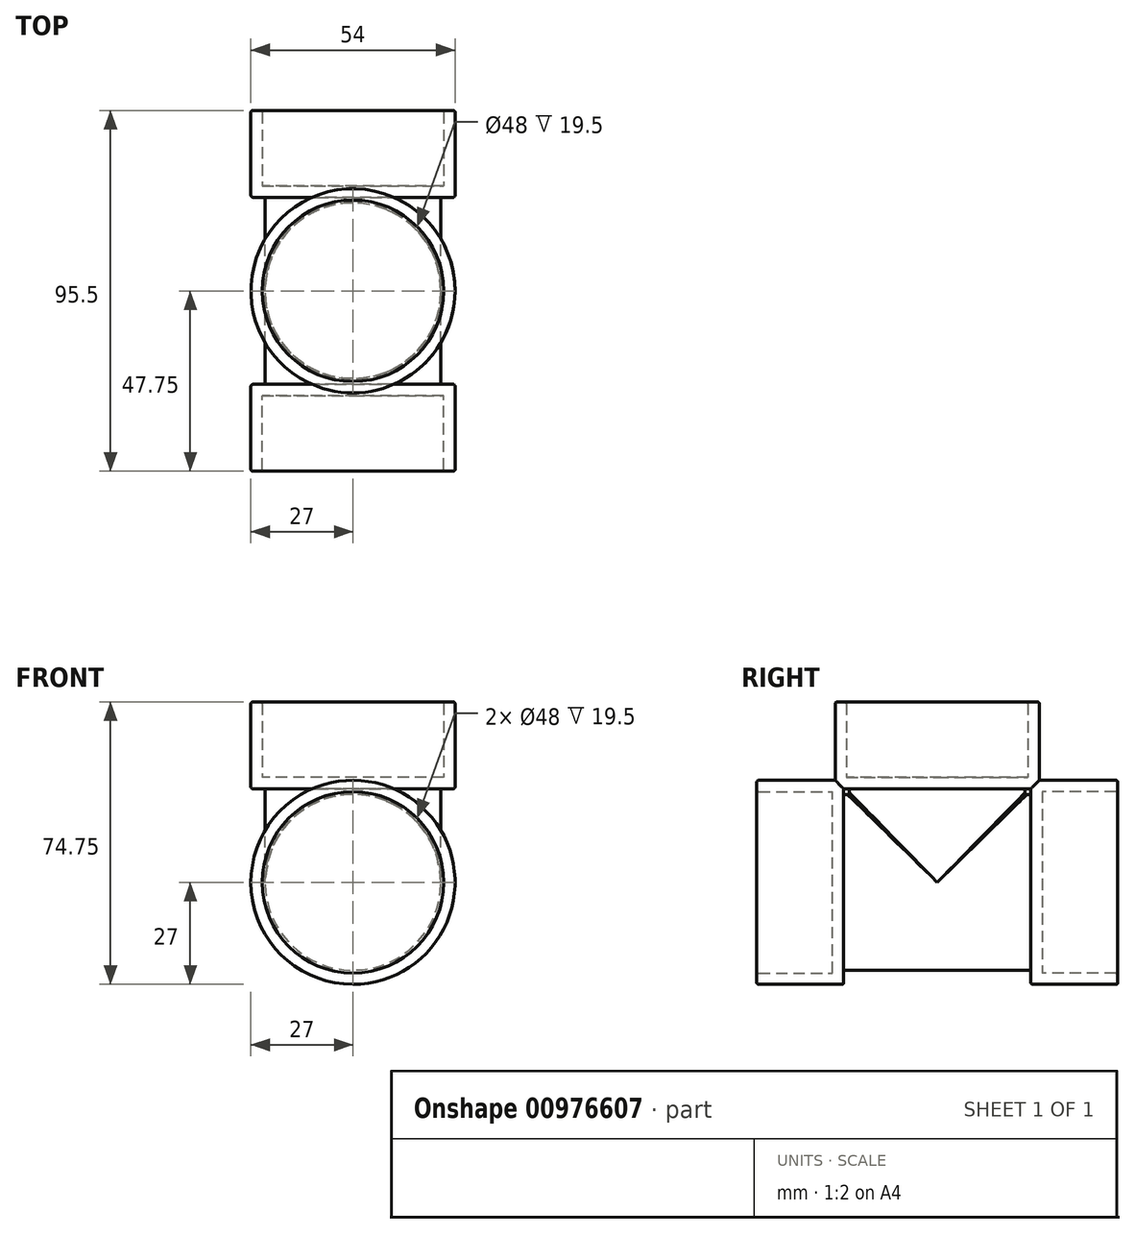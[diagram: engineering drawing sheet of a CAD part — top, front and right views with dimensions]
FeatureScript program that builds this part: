
annotation { "Feature Type Name" : "Feature", "Feature Type Description" : "" }
export const myFeature = defineFeature(function(context is Context, id is Id, definition is map)
    precondition{}
    {
        {
            var Q0;
            Q0=qCreatedBy(makeId("Right.planeOp"),FACE);
            var sketch = newSketch(context, id + "F0", { "sketchPlane" : qUnion([Q0])});
            skLineSegment(sketch, "E0.bottom", {"start": v(-22.5, 23.25) * mm, "end": v(-24, 23.25) * mm});
            skLineSegment(sketch, "E0.right", {"start": v(-24, 23.25) * mm, "end": v(-24, -23.25) * mm});
            skPoint(sketch, "E0.middle", {"position": v(0, 0) * mm});
            skLineSegment(sketch, "E1.top", {"start": v(24, 24.75) * mm, "end": v(-22.5, 24.75) * mm});
            skLineSegment(sketch, "E1.left", {"start": v(24, 23.25) * mm, "end": v(24, 24.75) * mm});
            skLineSegment(sketch, "E1.right", {"start": v(-22.5, 23.25) * mm, "end": v(-22.5, 24.75) * mm});
            skPoint(sketch, "E1.bottom.start.orphan", {"position": v(24, -23.25) * mm});
            skLineSegment(sketch, "E2", {"start": v(24, 23.25) * mm, "end": v(25.5, 23.25) * mm});
            skLineSegment(sketch, "E3", {"start": v(25.5, 23.25) * mm, "end": v(25.5, -23.25) * mm});
            skLineSegment(sketch, "E4", {"start": v(-24, -23.25) * mm, "end": v(25.5, -23.25) * mm});
            skSolve(sketch);
        }
        {
            var Q0;
            Q0=makeQuery(id+"F0.imprint","IMPRINT",FACE,{"disambiguationData":[TD([[makeQuery(id+"F0.imprint","IMPRINT",EDGE,{"derivedFrom":sQuery(id+"F0.wireOp",EDGE,"E0.bottom")}),1.0]])]});
            extrude(context, id + "F1", {"entities" : qUnion([Q0]), "depth" : 46.5 * mm, "offsetDistance" : 25 * mm});
        }
        {
            var Q0;
            Q0=makeQuery(id+"F1.opExtrude","CAP_EDGE",EDGE,{"disambiguationData":[OSD([sQuery(id+"F0.wireOp",EDGE,"E1.right")])],"isStart":false});
            var Q1;
            Q1=makeQuery(id+"F1.opExtrude","CAP_EDGE",EDGE,{"disambiguationData":[OSD([sQuery(id+"F0.wireOp",EDGE,"E0.bottom")])],"isStart":false});
            var Q2;
            Q2=makeQuery(id+"F1.opExtrude","CAP_EDGE",EDGE,{"disambiguationData":[OSD([sQuery(id+"F0.wireOp",EDGE,"E0.bottom")])],"isStart":true});
            var Q3;
            Q3=makeQuery(id+"F1.opExtrude","CAP_EDGE",EDGE,{"disambiguationData":[OSD([sQuery(id+"F0.wireOp",EDGE,"E1.right")])],"isStart":true});
            var Q4;
            Q4=makeQuery(id+"F1.opExtrude","CAP_EDGE",EDGE,{"disambiguationData":[OSD([sQuery(id+"F0.wireOp",EDGE,"E0.top"),sQuery(id+"F0.wireOp",EDGE,"E1.bottom")])],"isStart":true});
            var Q5;
            Q5=makeQuery(id+"F1.opExtrude","CAP_EDGE",EDGE,{"disambiguationData":[OSD([sQuery(id+"F0.wireOp",EDGE,"E1.left")])],"isStart":true});
            var Q6;
            Q6=makeQuery(id+"F1.opExtrude","CAP_EDGE",EDGE,{"disambiguationData":[OSD([sQuery(id+"F0.wireOp",EDGE,"E1.left")])],"isStart":false});
            var Q7;
            Q7=makeQuery(id+"F1.opExtrude","CAP_EDGE",EDGE,{"disambiguationData":[OSD([sQuery(id+"F0.wireOp",EDGE,"E0.top"),sQuery(id+"F0.wireOp",EDGE,"E1.bottom")])],"isStart":false});
            var Q8;
            Q8=makeQuery(id+"F1.opExtrude","CAP_EDGE",EDGE,{"disambiguationData":[OSD([sQuery(id+"F0.wireOp",EDGE,"rKhK8Vj8-QIDx-pT06-vwu7-Rd0EUUnwVlHf")])],"isStart":false});
            var Q9;
            Q9=makeQuery(id+"F1.opExtrude","CAP_EDGE",EDGE,{"disambiguationData":[OSD([sQuery(id+"F0.wireOp",EDGE,"rKhK8Vj8-QIDx-pT06-vwu7-Rd0EUUnwVlHf")])],"isStart":true});
            var Q10;
            Q10=makeQuery(id+"F1.opExtrude","CAP_EDGE",EDGE,{"disambiguationData":[OSD([sQuery(id+"F0.wireOp",EDGE,"E2")])],"isStart":true});
            var Q11;
            Q11=makeQuery(id+"F1.opExtrude","CAP_EDGE",EDGE,{"disambiguationData":[OSD([sQuery(id+"F0.wireOp",EDGE,"E2")])],"isStart":false});
            var Q12;
            Q12=makeQuery(id+"F1.opExtrude","CAP_EDGE",EDGE,{"disambiguationData":[OSD([sQuery(id+"F0.wireOp",EDGE,"E4")])],"isStart":false});
            var Q13;
            Q13=makeQuery(id+"F1.opExtrude","CAP_EDGE",EDGE,{"disambiguationData":[OSD([sQuery(id+"F0.wireOp",EDGE,"E4")])],"isStart":true});
            fillet(context, id + "F2", {"entities" : qUnion([Q0, Q1, Q2, Q3, Q4, Q5, Q6, Q7, Q8, Q9, Q10, Q11, Q12, Q13]), "radius" : 23.25 * mm, "tangentPropagation" : true, "allowEdgeOverflow" : false});
        }
        {
            var Q0;
            Q0=makeQuery(id+"F1.opExtrude","SWEPT_FACE",FACE,{"disambiguationData":[OSD([sQuery(id+"F0.wireOp",EDGE,"E1.top")])]});
            var sketch = newSketch(context, id + "F3", { "sketchPlane" : qUnion([Q0])});
            skCircle(sketch, "E5", {"center": v(23.25, 0.75) * mm, "radius": 27 * mm});
            skCircle(sketch, "E6", {"center": v(23.25, 0.75) * mm, "radius": 24 * mm});
            skCircle(sketch, "E7", {"center": v(23.25, 0.75) * mm, "radius": 20 * mm});
            skSolve(sketch);
        }
        {
            var Q0;
            Q0=makeQuery(id+"F1.opExtrude","SWEPT_FACE",FACE,{"disambiguationData":[OSD([sQuery(id+"F0.wireOp",EDGE,"E0.right")])]});
            var sketch = newSketch(context, id + "F4", { "sketchPlane" : qUnion([Q0])});
            skCircle(sketch, "E8", {"center": v(23.25, 0) * mm, "radius": 27 * mm});
            skCircle(sketch, "E9", {"center": v(23.25, 0) * mm, "radius": 24 * mm});
            skCircle(sketch, "E10", {"center": v(23.25, 0) * mm, "radius": 20 * mm});
            skSolve(sketch);
        }
        {
            var Q0;
            Q0=makeQuery(id+"F3.imprint","IMPRINT",FACE,{"disambiguationData":[TD([[makeQuery(id+"F3.imprint","IMPRINT",EDGE,{"derivedFrom":sQuery(id+"F3.wireOp",EDGE,"E7")}),-1.0]])]});
            var Q1;
            Q1=makeQuery(id+"F3.imprint","IMPRINT",FACE,{"disambiguationData":[TD([[makeQuery(id+"F3.imprint","IMPRINT",EDGE,{"derivedFrom":sQuery(id+"F3.wireOp",EDGE,"E6")}),1.0]])]});
            extrude(context, id + "F5", {"entities" : qUnion([Q0, Q1]), "operationType" : NewBodyOperationType.ADD, "depth" : 3 * mm, "offsetDistance" : 25 * mm});
        }
        {
            var Q0;
            Q0=makeQuery(id+"F3.imprint","IMPRINT",FACE,{"disambiguationData":[TD([[makeQuery(id+"F3.imprint","IMPRINT",EDGE,{"derivedFrom":sQuery(id+"F3.wireOp",EDGE,"E5")}),1.0]])]});
            extrude(context, id + "F6", {"entities" : qUnion([Q0]), "operationType" : NewBodyOperationType.ADD, "depth" : 23 * mm, "offsetDistance" : 25 * mm});
        }
        {
            var Q0;
            Q0=makeQuery(id+"F4.imprint","IMPRINT",FACE,{"disambiguationData":[TD([[makeQuery(id+"F4.imprint","IMPRINT",EDGE,{"derivedFrom":sQuery(id+"F4.wireOp",EDGE,"E10")}),-1.0]])]});
            var Q1;
            Q1=makeQuery(id+"F4.imprint","IMPRINT",FACE,{"disambiguationData":[TD([[makeQuery(id+"F4.imprint","IMPRINT",EDGE,{"derivedFrom":sQuery(id+"F4.wireOp",EDGE,"E9")}),1.0]])]});
            extrude(context, id + "F7", {"entities" : qUnion([Q0, Q1]), "operationType" : NewBodyOperationType.ADD, "depth" : 3 * mm, "offsetDistance" : 25 * mm});
        }
        {
            var Q0;
            Q0=makeQuery(id+"F4.imprint","IMPRINT",FACE,{"disambiguationData":[TD([[makeQuery(id+"F4.imprint","IMPRINT",EDGE,{"derivedFrom":sQuery(id+"F4.wireOp",EDGE,"E8")}),1.0]])]});
            extrude(context, id + "F8", {"entities" : qUnion([Q0]), "operationType" : NewBodyOperationType.ADD, "depth" : 23 * mm, "offsetDistance" : 25 * mm});
        }
        {
            var Q0;
            Q0=makeQuery(id+"F1.opExtrude","SWEPT_FACE",FACE,{"disambiguationData":[OSD([sQuery(id+"F0.wireOp",EDGE,"E3")])]});
            var sketch = newSketch(context, id + "F9", { "sketchPlane" : qUnion([Q0])});
            skCircle(sketch, "E11", {"center": v(-23.25, 0) * mm, "radius": 27 * mm});
            skCircle(sketch, "E12", {"center": v(-23.25, 0) * mm, "radius": 24 * mm});
            skCircle(sketch, "E13", {"center": v(-23.25, 0) * mm, "radius": 23 * mm});
            skSolve(sketch);
        }
        {
            var Q0;
            Q0=makeQuery(id+"F9.imprint","IMPRINT",FACE,{"disambiguationData":[TD([[makeQuery(id+"F9.imprint","IMPRINT",EDGE,{"derivedFrom":sQuery(id+"F9.wireOp",EDGE,"E12")}),1.0]])]});
            var Q1;
            Q1=makeQuery(id+"F9.imprint","IMPRINT",FACE,{"disambiguationData":[TD([[makeQuery(id+"F9.imprint","IMPRINT",EDGE,{"derivedFrom":sQuery(id+"F9.wireOp",EDGE,"E13")}),-1.0]])]});
            extrude(context, id + "F10", {"entities" : qUnion([Q0, Q1]), "operationType" : NewBodyOperationType.ADD, "depth" : 3 * mm, "offsetDistance" : 25 * mm});
        }
        {
            var Q0;
            Q0=makeQuery(id+"F9.imprint","IMPRINT",FACE,{"disambiguationData":[TD([[makeQuery(id+"F9.imprint","IMPRINT",EDGE,{"derivedFrom":sQuery(id+"F9.wireOp",EDGE,"E11")}),1.0]])]});
            extrude(context, id + "F11", {"entities" : qUnion([Q0]), "operationType" : NewBodyOperationType.ADD, "depth" : 23 * mm, "offsetDistance" : 25 * mm});
        }
        {
            var Q0;
            Q0=makeQuery(id+"F8.opExtrude","CAP_EDGE",EDGE,{"disambiguationData":[OSD([sQuery(id+"F4.wireOp",EDGE,"E8")])],"isStart":true});
            var Q1;
            Q1=makeQuery(id+"F6.opExtrude","CAP_EDGE",EDGE,{"disambiguationData":[OSD([sQuery(id+"F3.wireOp",EDGE,"E5")])],"isStart":true});
            var Q2;
            Q2=makeQuery(id+"F8.opExtrude","CAP_FACE",FACE,{"disambiguationData":[OSD([sQuery(id+"F4.wireOp",EDGE,"E8"),sQuery(id+"F4.wireOp",EDGE,"E9")])],"isStart":false});
            var Q3;
            Q3=makeQuery(id+"F6.opExtrude","CAP_FACE",FACE,{"disambiguationData":[OSD([sQuery(id+"F3.wireOp",EDGE,"E5"),sQuery(id+"F3.wireOp",EDGE,"E6")])],"isStart":false});
            var Q4;
            Q4=makeQuery(id+"F5.opExtrude","CAP_EDGE",EDGE,{"disambiguationData":[OSD([sQuery(id+"F3.wireOp",EDGE,"E6")])],"isStart":false});
            var Q5;
            Q5=makeQuery(id+"F7.opExtrude","CAP_EDGE",EDGE,{"disambiguationData":[OSD([sQuery(id+"F4.wireOp",EDGE,"E9")])],"isStart":false});
            fillet(context, id + "F12", {"entities" : qUnion([Q0, Q1, Q2, Q3, Q4, Q5]), "radius" : .5 * mm, "tangentPropagation" : true, "allowEdgeOverflow" : false});
        }
        {
            var Q0;
            Q0=makeQuery(id+"F11.opExtrude","CAP_FACE",FACE,{"disambiguationData":[OSD([sQuery(id+"F9.wireOp",EDGE,"E11"),sQuery(id+"F9.wireOp",EDGE,"E12")])],"isStart":false});
            var Q1;
            Q1=makeQuery(id+"F11.opExtrude","CAP_EDGE",EDGE,{"disambiguationData":[OSD([sQuery(id+"F9.wireOp",EDGE,"E11")])],"isStart":true});
            var Q2;
            Q2=makeQuery(id+"F2.opFillet","BLEND_EDGE",EDGE,{"blendedFrom":[makeQuery(id+"F1.opExtrude","CAP_EDGE",EDGE,{"disambiguationData":[OSD([sQuery(id+"F0.wireOp",EDGE,"E2")])],"isStart":true}),makeQuery(id+"F1.opExtrude","SWEPT_FACE",FACE,{"disambiguationData":[OSD([sQuery(id+"F0.wireOp",EDGE,"E3")])]})],"blendedInto":[makeQuery(id+"F1.opExtrude","SWEPT_FACE",FACE,{"disambiguationData":[OSD([sQuery(id+"F0.wireOp",EDGE,"E3")])]})]});
            var Q3;
            Q3=makeQuery(id+"F2.opFillet","BLEND_EDGE",EDGE,{"blendedFrom":[makeQuery(id+"F1.opExtrude","CAP_EDGE",EDGE,{"disambiguationData":[OSD([sQuery(id+"F0.wireOp",EDGE,"E1.left")])],"isStart":true}),makeQuery(id+"F1.opExtrude","CAP_EDGE",EDGE,{"disambiguationData":[OSD([sQuery(id+"F0.wireOp",EDGE,"E2")])],"isStart":true})],"blendedInto":[]});
            var Q4;
            Q4=makeQuery(id+"F2.opFillet","BLEND_EDGE",EDGE,{"blendedFrom":[makeQuery(id+"F1.opExtrude","CAP_EDGE",EDGE,{"disambiguationData":[OSD([sQuery(id+"F0.wireOp",EDGE,"E0.bottom")])],"isStart":true}),makeQuery(id+"F1.opExtrude","CAP_EDGE",EDGE,{"disambiguationData":[OSD([sQuery(id+"F0.wireOp",EDGE,"E1.right")])],"isStart":true})],"blendedInto":[]});
            var Q5;
            Q5=makeQuery(id+"F2.opFillet","BLEND_EDGE",EDGE,{"blendedFrom":[makeQuery(id+"F1.opExtrude","CAP_EDGE",EDGE,{"disambiguationData":[OSD([sQuery(id+"F0.wireOp",EDGE,"E1.left")])],"isStart":true}),makeQuery(id+"F1.opExtrude","SWEPT_FACE",FACE,{"disambiguationData":[OSD([sQuery(id+"F0.wireOp",EDGE,"E1.top")])]})],"blendedInto":[makeQuery(id+"F1.opExtrude","SWEPT_FACE",FACE,{"disambiguationData":[OSD([sQuery(id+"F0.wireOp",EDGE,"E1.top")])]})]});
            var Q6;
            Q6=makeQuery(id+"F2.opFillet","BLEND_EDGE",EDGE,{"blendedFrom":[makeQuery(id+"F1.opExtrude","CAP_EDGE",EDGE,{"disambiguationData":[OSD([sQuery(id+"F0.wireOp",EDGE,"E0.bottom")])],"isStart":true}),makeQuery(id+"F1.opExtrude","SWEPT_FACE",FACE,{"disambiguationData":[OSD([sQuery(id+"F0.wireOp",EDGE,"E0.right")])]})],"blendedInto":[makeQuery(id+"F1.opExtrude","SWEPT_FACE",FACE,{"disambiguationData":[OSD([sQuery(id+"F0.wireOp",EDGE,"E0.right")])]})]});
            fillet(context, id + "F13", {"entities" : qUnion([Q0, Q1, Q2, Q3, Q4, Q5, Q6]), "radius" : .5 * mm, "tangentPropagation" : true, "allowEdgeOverflow" : false});
        }
        {
            var Q0;
            Q0=makeQuery(id+"F9.imprint","IMPRINT",FACE,{"disambiguationData":[TD([[makeQuery(id+"F9.imprint","IMPRINT",EDGE,{"derivedFrom":sQuery(id+"F9.wireOp",EDGE,"E13")}),1.0]])]});
            extrude(context, id + "F14", {"entities" : qUnion([Q0]), "operationType" : NewBodyOperationType.ADD, "depth" : 3 * mm, "offsetDistance" : 25 * mm});
        }
        {
            var Q0;
            Q0=makeQuery(id+"F3.imprint","IMPRINT",FACE,{"disambiguationData":[TD([[makeQuery(id+"F3.imprint","IMPRINT",EDGE,{"derivedFrom":sQuery(id+"F3.wireOp",EDGE,"E7")}),1.0]])]});
            extrude(context, id + "F15", {"entities" : qUnion([Q0]), "operationType" : NewBodyOperationType.ADD, "depth" : 3 * mm, "offsetDistance" : 25 * mm});
        }
        {
            var Q0;
            Q0=makeQuery(id+"F4.imprint","IMPRINT",FACE,{"disambiguationData":[TD([[makeQuery(id+"F4.imprint","IMPRINT",EDGE,{"derivedFrom":sQuery(id+"F4.wireOp",EDGE,"E10")}),1.0]])]});
            extrude(context, id + "F16", {"entities" : qUnion([Q0]), "operationType" : NewBodyOperationType.ADD, "depth" : 3 * mm, "offsetDistance" : 25 * mm});
        }
    });
